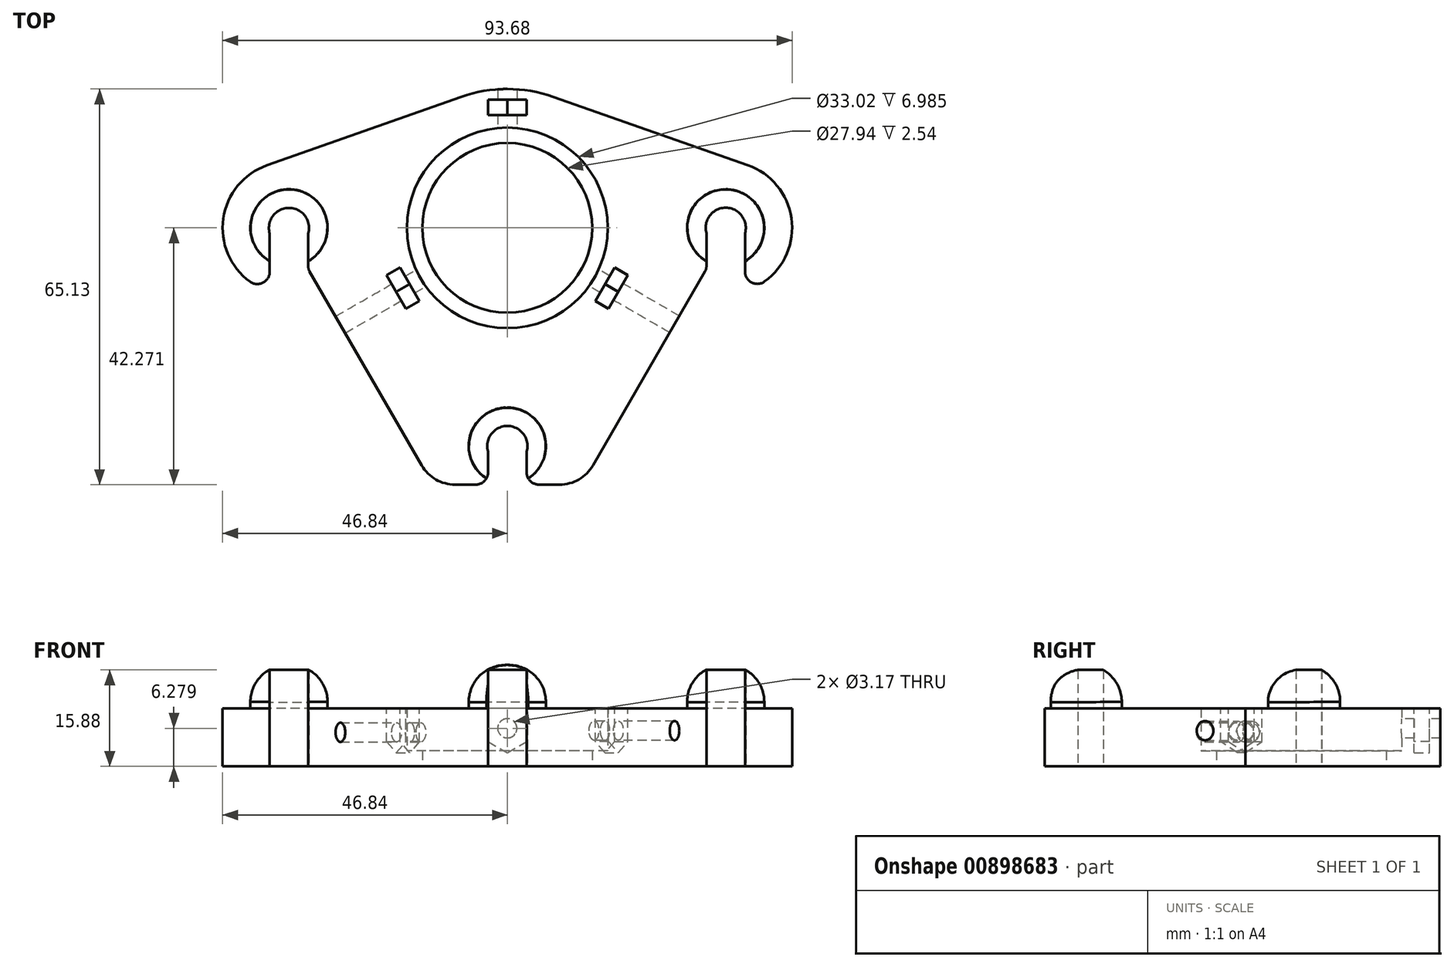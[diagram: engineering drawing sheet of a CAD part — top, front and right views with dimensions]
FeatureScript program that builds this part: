
annotation { "Feature Type Name" : "Feature", "Feature Type Description" : "" }
export const myFeature = defineFeature(function(context is Context, id is Id, definition is map)
    precondition{}
    {
        {
            var Q0;
            Q0=qCreatedBy(makeId("Top.planeOp"),FACE);
            var sketch = newSketch(context, id + "F0", { "sketchPlane" : qUnion([Q0])});
            skCircle(sketch, "E0", {"center": v(0, 35.92) * mm, "radius": 16.51 * mm});
            skArc(sketch, "E1.0", {"start": v(-39.55, 46.2) * mm, "mid": v(-46.73, 37.47) * mm, "end": v(-42.32, 27.05) * mm});
            skArc(sketch, "E2.0", {"start": v(7.59, 57.48) * mm, "mid": v(0, 58.78) * mm, "end": v(-7.6, 57.48) * mm});
            skArc(sketch, "E3.0", {"start": v(42.32, 27.08) * mm, "mid": v(46.73, 37.5) * mm, "end": v(39.55, 46.24) * mm});
            skLineSegment(sketch, "E4", {"start": v(-39.55, 46.2) * mm, "end": v(-7.6, 57.48) * mm});
            skLineSegment(sketch, "E5", {"start": v(7.59, 57.48) * mm, "end": v(39.55, 46.24) * mm});
            skCircle(sketch, "E6", {"center": v(-35.92, 35.92) * mm, "radius": 3.18 * mm, "construction": true});
            skCircle(sketch, "E7", {"center": v(35.92, 35.92) * mm, "radius": 3.18 * mm, "construction": true});
            skCircle(sketch, "E8", {"center": v(0, 0) * mm, "radius": 3.18 * mm, "construction": true});
            skLineSegment(sketch, "E9", {"start": v(-32.75, 35.92) * mm, "end": v(-32.75, 29.55) * mm});
            skLineSegment(sketch, "E10", {"start": v(-39.1, 35.92) * mm, "end": v(-39.1, 28.7) * mm});
            skLineSegment(sketch, "E11", {"start": v(-3.18, 0) * mm, "end": v(-3.17, -4.32) * mm});
            skLineSegment(sketch, "E12", {"start": v(3.17, 0) * mm, "end": v(3.17, -4.32) * mm});
            skLineSegment(sketch, "E13", {"start": v(32.75, 35.92) * mm, "end": v(32.75, 29.55) * mm});
            skLineSegment(sketch, "E14", {"start": v(39.1, 35.92) * mm, "end": v(39.1, 28.73) * mm});
            skCircle(sketch, "E15.0", {"center": v(0, 35.92) * mm, "radius": 13.97 * mm});
            skLineSegment(sketch, "E16", {"start": v(0, 35.92) * mm, "end": v(0, 52.43) * mm, "construction": true});
            skLineSegment(sketch, "E17", {"start": v(0, 35.92) * mm, "end": v(35.3, 15.54) * mm, "construction": true});
            skLineSegment(sketch, "E18", {"start": v(0, 35.92) * mm, "end": v(-35.36, 15.5) * mm, "construction": true});
            skCircle(sketch, "E19.cCircle", {"center": v(0, 35.92) * mm, "radius": 16.51 * mm, "construction": true});
            skLineSegment(sketch, "E19.0", {"start": v(9.53, 52.43) * mm, "end": v(19.06, 35.92) * mm, "construction": true});
            skLineSegment(sketch, "E19.1", {"start": v(19.06, 35.92) * mm, "end": v(9.53, 19.41) * mm, "construction": true});
            skLineSegment(sketch, "E19.2", {"start": v(9.53, 19.41) * mm, "end": v(-9.53, 19.41) * mm, "construction": true});
            skLineSegment(sketch, "E19.3", {"start": v(-9.53, 19.41) * mm, "end": v(-19.06, 35.92) * mm, "construction": true});
            skLineSegment(sketch, "E19.4", {"start": v(-19.06, 35.92) * mm, "end": v(-9.53, 52.43) * mm, "construction": true});
            skLineSegment(sketch, "E19.5", {"start": v(-9.53, 52.43) * mm, "end": v(9.53, 52.43) * mm, "construction": true});
            skPoint(sketch, "E19.0.midPoint", {"position": v(14.3, 44.18) * mm});
            skLineSegment(sketch, "E20", {"start": v(-35.92, 35.92) * mm, "end": v(35.92, 35.92) * mm, "construction": true});
            skCircle(sketch, "E21.0", {"center": v(0, 35.92) * mm, "radius": 31.75 * mm, "construction": true});
            skLineSegment(sketch, "E22", {"start": v(-32.54, 28.79) * mm, "end": v(-14.09, -3.17) * mm});
            skLineSegment(sketch, "E23", {"start": v(32.54, 28.79) * mm, "end": v(14.09, -3.18) * mm});
            skPoint(sketch, "E24.visualSharp", {"position": v(-32.75, 29.14) * mm});
            skArc(sketch, "E24.filletArc", {"start": v(-32.75, 29.55) * mm, "mid": v(-32.7, 29.15) * mm, "end": v(-32.54, 28.79) * mm});
            skPoint(sketch, "E25.visualSharp", {"position": v(32.75, 29.14) * mm});
            skArc(sketch, "E25.filletArc", {"start": v(32.54, 28.79) * mm, "mid": v(32.7, 29.15) * mm, "end": v(32.75, 29.55) * mm});
            skArc(sketch, "E26", {"start": v(3.17, -0.9) * mm, "mid": v(0, 3.3) * mm, "end": v(-3.18, -0.9) * mm});
            skArc(sketch, "E27", {"start": v(-32.75, 35) * mm, "mid": v(-35.92, 39.2) * mm, "end": v(-39.1, 35) * mm});
            skArc(sketch, "E28", {"start": v(39.1, 35.03) * mm, "mid": v(35.92, 39.24) * mm, "end": v(32.75, 35.03) * mm});
            skLineSegment(sketch, "E29", {"start": v(-8.6, -6.35) * mm, "end": v(-5.2, -6.35) * mm});
            skLineSegment(sketch, "E30.trimOffspring", {"start": v(5.2, -6.35) * mm, "end": v(8.6, -6.35) * mm});
            skPoint(sketch, "E31.visualSharp", {"position": v(-12.26, -6.35) * mm});
            skArc(sketch, "E31.filletArc", {"start": v(-14.09, -3.17) * mm, "mid": v(-11.77, -5.5) * mm, "end": v(-8.6, -6.35) * mm});
            skPoint(sketch, "E32.visualSharp", {"position": v(12.26, -6.35) * mm});
            skArc(sketch, "E32.filletArc", {"start": v(8.6, -6.35) * mm, "mid": v(11.77, -5.5) * mm, "end": v(14.09, -3.18) * mm});
            skPoint(sketch, "E33.visualSharp", {"position": v(-3.17, -6.35) * mm});
            skArc(sketch, "E33.filletArc", {"start": v(-5.2, -6.35) * mm, "mid": v(-3.77, -5.75) * mm, "end": v(-3.18, -4.32) * mm});
            skPoint(sketch, "E34.visualSharp", {"position": v(3.18, -6.35) * mm});
            skArc(sketch, "E34.filletArc", {"start": v(3.17, -4.32) * mm, "mid": v(3.77, -5.75) * mm, "end": v(5.2, -6.35) * mm});
            skPoint(sketch, "E35.visualSharp", {"position": v(-39.1, 25.46) * mm});
            skArc(sketch, "E35.filletArc", {"start": v(-42.32, 27.05) * mm, "mid": v(-40.2, 26.9) * mm, "end": v(-39.1, 28.7) * mm});
            skPoint(sketch, "E36.visualSharp", {"position": v(39.1, 25.49) * mm});
            skArc(sketch, "E36.filletArc", {"start": v(39.1, 28.73) * mm, "mid": v(40.2, 26.92) * mm, "end": v(42.32, 27.08) * mm});
            skSolve(sketch);
        }
        {
            var Q0;
            Q0=makeQuery(id+"F0.imprint","IMPRINT",FACE,{"disambiguationData":[TD([[makeQuery(id+"F0.imprint","IMPRINT",EDGE,{"derivedFrom":sQuery(id+"F0.wireOp",EDGE,"E0")}),-1.0]])]});
            extrude(context, id + "F1", {"entities" : qUnion([Q0]), "depth" : 9.52 * mm, "offsetDistance" : 25.4 * mm});
        }
        {
            var Q0;
            Q0=makeQuery(id+"F0.imprint","IMPRINT",FACE,{"disambiguationData":[TD([[makeQuery(id+"F0.imprint","IMPRINT",EDGE,{"derivedFrom":sQuery(id+"F0.wireOp",EDGE,"E0")}),1.0]])]});
            extrude(context, id + "F2", {"entities" : qUnion([Q0]), "operationType" : NewBodyOperationType.ADD, "depth" : 2.54 * mm, "hasOffset" : true, "offsetDistance" : 6.35 * mm});
        }
        {
            var Q0;
            Q0=makeQuery(id+"F1.opExtrude","CAP_FACE",FACE,{"disambiguationData":[OSD([sQuery(id+"F0.wireOp",EDGE,"EjYE8rPL-0voM-13ep-dpKR-Yhmu4oC0fMjX"),sQuery(id+"F0.wireOp",EDGE,"BDsdlpYl-4XZS-kb72-SQzJ-jy24um5DGsSm"),sQuery(id+"F0.wireOp",EDGE,"zDj9rnkT-zBYQ-YRrf-FuGE-prHvdQQL9E0l"),sQuery(id+"F0.wireOp",EDGE,"E0"),sQuery(id+"F0.wireOp",EDGE,"E1.0"),sQuery(id+"F0.wireOp",EDGE,"E2.0"),sQuery(id+"F0.wireOp",EDGE,"E3.0"),sQuery(id+"F0.wireOp",EDGE,"02fbeba7-076e-4ed0-9f02-67362b93dccf.0"),sQuery(id+"F0.wireOp",EDGE,"E4"),sQuery(id+"F0.wireOp",EDGE,"E5"),sQuery(id+"F0.wireOp",EDGE,"O9yRHGw0-B6N5-WUBC-CqYZ-9fVMz9zkHXct"),sQuery(id+"F0.wireOp",EDGE,"bXI39tXD-kIKO-QA8d-uo1d-AjNWw4kzWSzn"),sQuery(id+"F0.wireOp",EDGE,"E9"),sQuery(id+"F0.wireOp",EDGE,"E10"),sQuery(id+"F0.wireOp",EDGE,"E11"),sQuery(id+"F0.wireOp",EDGE,"E12"),sQuery(id+"F0.wireOp",EDGE,"1b80de2d-6fcf-4166-8bd7-bc7520118ab3.trimOffspring"),sQuery(id+"F0.wireOp",EDGE,"c2b8b45b-57a7-46a8-b7ff-993cbbd2993e.trimOffspring"),sQuery(id+"F0.wireOp",EDGE,"9e57da74-859c-4f91-937b-fdcaf8afdda5.filletArc"),sQuery(id+"F0.wireOp",EDGE,"30e6a12d-ff62-4460-809b-2951cf116d4f.filletArc"),sQuery(id+"F0.wireOp",EDGE,"3d167f00-72a4-4ff5-8a6d-0d591a0e7773.filletArc"),sQuery(id+"F0.wireOp",EDGE,"E13"),sQuery(id+"F0.wireOp",EDGE,"E14"),sQuery(id+"F0.wireOp",EDGE,"02ed80ea-b338-46f1-988c-5186e078d909.trimOffspring"),sQuery(id+"F0.wireOp",EDGE,"3LgmcLzA-5pnU-fFz7-q1u9-bpeBtAsCO3An"),sQuery(id+"F0.wireOp",EDGE,"4eo9xTR6-c1Fu-en91-zOid-S4E7wj55DmDX"),sQuery(id+"F0.wireOp",EDGE,"5048e359-dd0b-4d89-8e95-103b38747b91.filletArc"),sQuery(id+"F0.wireOp",EDGE,"0de4be46-af92-408f-a28e-b5eb566cc358.filletArc"),sQuery(id+"F0.wireOp",EDGE,"cd97e584-8722-4711-bad1-4d169eb79cda.filletArc"),sQuery(id+"F0.wireOp",EDGE,"a80f9f6f-3806-41d0-9fd0-596e0330244b.filletArc"),sQuery(id+"F0.wireOp",EDGE,"743a1c7c-530f-41f0-bede-06812bb20fe3.filletArc")])],"isStart":false});
            var sketch = newSketch(context, id + "F3", { "sketchPlane" : qUnion([Q0])});
            skCircle(sketch, "E37", {"center": v(-35.92, 35.92) * mm, "radius": 6.35 * mm});
            skCircle(sketch, "E38", {"center": v(35.92, 35.92) * mm, "radius": 6.35 * mm});
            skCircle(sketch, "E39", {"center": v(0, 0) * mm, "radius": 6.35 * mm});
            skSolve(sketch);
        }
        {
            var Q0;
            Q0=makeQuery(id+"F1.opExtrude","CAP_FACE",FACE,{"disambiguationData":[OSD([sQuery(id+"F0.wireOp",EDGE,"EjYE8rPL-0voM-13ep-dpKR-Yhmu4oC0fMjX"),sQuery(id+"F0.wireOp",EDGE,"BDsdlpYl-4XZS-kb72-SQzJ-jy24um5DGsSm"),sQuery(id+"F0.wireOp",EDGE,"zDj9rnkT-zBYQ-YRrf-FuGE-prHvdQQL9E0l"),sQuery(id+"F0.wireOp",EDGE,"E0"),sQuery(id+"F0.wireOp",EDGE,"E1.0"),sQuery(id+"F0.wireOp",EDGE,"E2.0"),sQuery(id+"F0.wireOp",EDGE,"E3.0"),sQuery(id+"F0.wireOp",EDGE,"02fbeba7-076e-4ed0-9f02-67362b93dccf.0"),sQuery(id+"F0.wireOp",EDGE,"E4"),sQuery(id+"F0.wireOp",EDGE,"E5"),sQuery(id+"F0.wireOp",EDGE,"O9yRHGw0-B6N5-WUBC-CqYZ-9fVMz9zkHXct"),sQuery(id+"F0.wireOp",EDGE,"bXI39tXD-kIKO-QA8d-uo1d-AjNWw4kzWSzn"),sQuery(id+"F0.wireOp",EDGE,"E9"),sQuery(id+"F0.wireOp",EDGE,"E10"),sQuery(id+"F0.wireOp",EDGE,"E11"),sQuery(id+"F0.wireOp",EDGE,"E12"),sQuery(id+"F0.wireOp",EDGE,"1b80de2d-6fcf-4166-8bd7-bc7520118ab3.trimOffspring"),sQuery(id+"F0.wireOp",EDGE,"c2b8b45b-57a7-46a8-b7ff-993cbbd2993e.trimOffspring"),sQuery(id+"F0.wireOp",EDGE,"9e57da74-859c-4f91-937b-fdcaf8afdda5.filletArc"),sQuery(id+"F0.wireOp",EDGE,"2f08ad09-a47d-42bd-8f0e-b7f58f6490e4.filletArc"),sQuery(id+"F0.wireOp",EDGE,"30e6a12d-ff62-4460-809b-2951cf116d4f.filletArc"),sQuery(id+"F0.wireOp",EDGE,"3d167f00-72a4-4ff5-8a6d-0d591a0e7773.filletArc"),sQuery(id+"F0.wireOp",EDGE,"E13"),sQuery(id+"F0.wireOp",EDGE,"E14"),sQuery(id+"F0.wireOp",EDGE,"02ed80ea-b338-46f1-988c-5186e078d909.trimOffspring"),sQuery(id+"F0.wireOp",EDGE,"bfc3d6b4-ed7b-404a-8939-94d15189dd00.filletArc"),sQuery(id+"F0.wireOp",EDGE,"d06de643-c4a7-4e1d-b592-4d839de3a7a0.filletArc")])],"isStart":false});
            var sketch = newSketch(context, id + "F4", { "sketchPlane" : qUnion([Q0])});
            skLineSegment(sketch, "E40", {"start": v(-3.18, 54.46) * mm, "end": v(-3.18, 57) * mm});
            skLineSegment(sketch, "E41", {"start": v(-3.18, 57) * mm, "end": v(3.17, 57) * mm});
            skLineSegment(sketch, "E42", {"start": v(3.17, 57) * mm, "end": v(3.17, 54.46) * mm});
            skLineSegment(sketch, "E43", {"start": v(3.18, 54.46) * mm, "end": v(-3.18, 54.46) * mm});
            skLineSegment(sketch, "E44", {"start": v(0, 52.43) * mm, "end": v(0, 54.46) * mm});
            skLineSegment(sketch, "E45.1.0", {"start": v(-17.65, 29.4) * mm, "end": v(-14.47, 23.9) * mm});
            skLineSegment(sketch, "E45.1.1", {"start": v(-19.85, 28.13) * mm, "end": v(-17.65, 29.4) * mm});
            skLineSegment(sketch, "E45.1.2", {"start": v(-16.67, 22.63) * mm, "end": v(-19.85, 28.13) * mm});
            skLineSegment(sketch, "E45.1.3", {"start": v(-14.47, 23.9) * mm, "end": v(-16.67, 22.63) * mm});
            skLineSegment(sketch, "E45.2.0", {"start": v(14.47, 23.9) * mm, "end": v(17.65, 29.4) * mm});
            skLineSegment(sketch, "E45.2.1", {"start": v(16.67, 22.63) * mm, "end": v(14.47, 23.9) * mm});
            skLineSegment(sketch, "E45.2.2", {"start": v(19.85, 28.13) * mm, "end": v(16.67, 22.63) * mm});
            skLineSegment(sketch, "E45.2.3", {"start": v(17.65, 29.4) * mm, "end": v(19.85, 28.13) * mm});
            skPoint(sketch, "E45.center", {"position": v(0, 35.92) * mm});
            skSolve(sketch);
        }
        {
            var Q0;
            Q0=makeQuery(id+"F4.imprint","IMPRINT",FACE,{"disambiguationData":[TD([[makeQuery(id+"F4.imprint","IMPRINT",EDGE,{"derivedFrom":sQuery(id+"F4.wireOp",EDGE,"E45.2.0")}),-1.0]])]});
            var Q1;
            {var subQ3=sQuery(id+"F4.wireOp",EDGE,"E40");Q1=makeQuery(id+"F4.imprint","IMPRINT",FACE,{"disambiguationData":[TD([[makeQuery(id+"F4.imprint","IMPRINT",EDGE,{"derivedFrom":subQ3}),-1.0]])]});}
            var Q2;
            Q2=makeQuery(id+"F4.imprint","IMPRINT",FACE,{"disambiguationData":[TD([[makeQuery(id+"F4.imprint","IMPRINT",EDGE,{"derivedFrom":sQuery(id+"F4.wireOp",EDGE,"E45.1.0")}),-1.0]])]});
            extrude(context, id + "F5", {"entities" : qUnion([Q0, Q1, Q2]), "operationType" : NewBodyOperationType.REMOVE, "oppositeDirection" : true, "depth" : 8.64 * mm, "offsetDistance" : 25.4 * mm});
        }
        {
            var Q0;
            Q0=makeQuery(id+"F5.boolean.opBoolean","COPY",EDGE,{"derivedFrom":makeQuery(id+"F5.opExtrude","CAP_EDGE",EDGE,{"disambiguationData":[OSD([sQuery(id+"F4.wireOp",EDGE,"E45.1.1")])],"isStart":false})});
            var Q1;
            Q1=makeQuery(id+"F5.boolean.opBoolean","COPY",EDGE,{"derivedFrom":makeQuery(id+"F5.opExtrude","CAP_EDGE",EDGE,{"disambiguationData":[OSD([sQuery(id+"F4.wireOp",EDGE,"E45.1.3")])],"isStart":false})});
            var Q2;
            Q2=makeQuery(id+"F5.boolean.opBoolean","COPY",EDGE,{"derivedFrom":makeQuery(id+"F5.opExtrude","CAP_EDGE",EDGE,{"disambiguationData":[OSD([sQuery(id+"F4.wireOp",EDGE,"E40")])],"isStart":false})});
            var Q3;
            Q3=makeQuery(id+"F5.boolean.opBoolean","COPY",EDGE,{"derivedFrom":makeQuery(id+"F5.opExtrude","CAP_EDGE",EDGE,{"disambiguationData":[OSD([sQuery(id+"F4.wireOp",EDGE,"E42")])],"isStart":false})});
            var Q4;
            Q4=makeQuery(id+"F5.boolean.opBoolean","COPY",EDGE,{"derivedFrom":makeQuery(id+"F5.opExtrude","CAP_EDGE",EDGE,{"disambiguationData":[OSD([sQuery(id+"F4.wireOp",EDGE,"E45.2.3")])],"isStart":false})});
            var Q5;
            Q5=makeQuery(id+"F5.boolean.opBoolean","COPY",EDGE,{"derivedFrom":makeQuery(id+"F5.opExtrude","CAP_EDGE",EDGE,{"disambiguationData":[OSD([sQuery(id+"F4.wireOp",EDGE,"E45.2.1")])],"isStart":false})});
            chamfer(context, id + "F6", {"entities" : qUnion([Q0, Q1, Q2, Q3, Q4, Q5]), "chamferType" : ChamferType.OFFSET_ANGLE, "width" : 3.17 * mm, "oppositeDirection" : false, "angle" : 60 * degree, "tangentPropagation" : true});
        }
        {
            var Q0;
            Q0=makeQuery(id+"F5.boolean.opBoolean","COPY",FACE,{"derivedFrom":makeQuery(id+"F5.opExtrude","SWEPT_FACE",FACE,{"disambiguationData":[OSD([sQuery(id+"F4.wireOp",EDGE,"E41")])]})});
            var sketch = newSketch(context, id + "F7", { "sketchPlane" : qUnion([Q0])});
            skLineSegment(sketch, "E46", {"start": v(3.17, 4.06) * mm, "end": v(0, 2.23) * mm});
            skLineSegment(sketch, "E47", {"start": v(0, 2.23) * mm, "end": v(-3.18, 4.06) * mm});
            skLineSegment(sketch, "E48", {"start": v(-3.17, 4.06) * mm, "end": v(-3.17, 7.73) * mm});
            skLineSegment(sketch, "E49", {"start": v(3.18, 7.73) * mm, "end": v(3.18, 4.06) * mm});
            skLineSegment(sketch, "E50", {"start": v(3.17, 7.73) * mm, "end": v(0, 9.55) * mm});
            skPoint(sketch, "E50.endSnap0", {"position": v(0, 9.53) * mm});
            skLineSegment(sketch, "E51", {"start": v(0, 9.55) * mm, "end": v(-3.17, 7.73) * mm});
            skLineSegment(sketch, "E52", {"start": v(0, 2.23) * mm, "end": v(0, 6.28) * mm, "construction": true});
            skLineSegment(sketch, "E53", {"start": v(0, 6.28) * mm, "end": v(3.17, 4.06) * mm, "construction": true});
            skLineSegment(sketch, "E54", {"start": v(0, 6.28) * mm, "end": v(-3.18, 4.06) * mm, "construction": true});
            skLineSegment(sketch, "E55", {"start": v(0, 6.28) * mm, "end": v(-3.17, 7.73) * mm, "construction": true});
            skLineSegment(sketch, "E56", {"start": v(0, 6.28) * mm, "end": v(3.17, 7.73) * mm, "construction": true});
            skLineSegment(sketch, "E57", {"start": v(0, 6.28) * mm, "end": v(0, 9.55) * mm, "construction": true});
            skCircle(sketch, "E58", {"center": v(0, 6.28) * mm, "radius": 1.59 * mm});
            skSolve(sketch);
        }
        {
            var Q0;
            Q0=makeQuery(id+"F5.boolean.opBoolean","COPY",FACE,{"derivedFrom":makeQuery(id+"F5.opExtrude","SWEPT_FACE",FACE,{"disambiguationData":[OSD([sQuery(id+"F4.wireOp",EDGE,"E45.1.2")])]})});
            var sketch = newSketch(context, id + "F8", { "sketchPlane" : qUnion([Q0])});
            skLineSegment(sketch, "E59", {"start": v(34.2, 3.78) * mm, "end": v(31.03, 1.94) * mm});
            skLineSegment(sketch, "E60", {"start": v(31.03, 1.94) * mm, "end": v(27.86, 3.78) * mm});
            skLineSegment(sketch, "E61", {"start": v(27.86, 3.78) * mm, "end": v(27.86, 7.44) * mm});
            skLineSegment(sketch, "E62", {"start": v(34.2, 7.44) * mm, "end": v(34.2, 3.78) * mm});
            skLineSegment(sketch, "E63", {"start": v(34.2, 7.44) * mm, "end": v(31.03, 9.26) * mm});
            skLineSegment(sketch, "E64", {"start": v(31.03, 9.26) * mm, "end": v(27.86, 7.44) * mm});
            skCircle(sketch, "E65", {"center": v(31.03, 5.6) * mm, "radius": 1.59 * mm});
            skSolve(sketch);
        }
        {
            var Q0;
            Q0=makeQuery(id+"F5.boolean.opBoolean","COPY",FACE,{"derivedFrom":makeQuery(id+"F5.opExtrude","SWEPT_FACE",FACE,{"disambiguationData":[OSD([sQuery(id+"F4.wireOp",EDGE,"E45.2.2")])]})});
            var sketch = newSketch(context, id + "F9", { "sketchPlane" : qUnion([Q0])});
            skLineSegment(sketch, "E66", {"start": v(-27.95, 4.06) * mm, "end": v(-31.12, 2.24) * mm});
            skLineSegment(sketch, "E67", {"start": v(-31.12, 2.24) * mm, "end": v(-34.28, 4.06) * mm});
            skLineSegment(sketch, "E68", {"start": v(-34.28, 4.06) * mm, "end": v(-34.28, 7.72) * mm});
            skLineSegment(sketch, "E69", {"start": v(-27.95, 7.72) * mm, "end": v(-27.95, 4.06) * mm});
            skLineSegment(sketch, "E70", {"start": v(-27.95, 7.72) * mm, "end": v(-31.12, 9.55) * mm});
            skLineSegment(sketch, "E71", {"start": v(-31.12, 9.55) * mm, "end": v(-34.28, 7.72) * mm});
            skCircle(sketch, "E72", {"center": v(-31.12, 5.9) * mm, "radius": 1.59 * mm});
            skLineSegment(sketch, "E73", {"start": v(-31.12, 2.24) * mm, "end": v(-31.12, 5.9) * mm, "construction": true});
            skLineSegment(sketch, "E74", {"start": v(-31.12, 5.9) * mm, "end": v(-34.28, 4.06) * mm, "construction": true});
            skLineSegment(sketch, "E75", {"start": v(-31.12, 9.55) * mm, "end": v(-31.12, 5.9) * mm, "construction": true});
            skLineSegment(sketch, "E76", {"start": v(-27.95, 7.72) * mm, "end": v(-31.12, 5.9) * mm, "construction": true});
            skSolve(sketch);
        }
        {
            var Q0;
            Q0=makeQuery(id+"F7.imprint","IMPRINT",FACE,{"disambiguationData":[TD([[makeQuery(id+"F7.imprint","IMPRINT",EDGE,{"derivedFrom":sQuery(id+"F7.wireOp",EDGE,"E58")}),1.0]])]});
            extrude(context, id + "F10", {"entities" : qUnion([Q0]), "operationType" : NewBodyOperationType.REMOVE, "oppositeDirection" : true, "depth" : 10.16 * mm, "offsetDistance" : 25.4 * mm, "symmetric" : true});
        }
        {
            var Q0;
            Q0=makeQuery(id+"F8.imprint","IMPRINT",FACE,{"disambiguationData":[TD([[makeQuery(id+"F8.imprint","IMPRINT",EDGE,{"derivedFrom":sQuery(id+"F8.wireOp",EDGE,"E65")}),1.0]])]});
            var Q1;
            Q1=sQuery(id+"F8.wireOp",EDGE,"E65");
            extrude(context, id + "F11", {"entities" : qUnion([Q0]), "operationType" : NewBodyOperationType.REMOVE, "surfaceEntities" : qUnion([Q1]), "oppositeDirection" : true, "depth" : 40.64 * mm, "offsetDistance" : 25.4 * mm, "symmetric" : true});
        }
        {
            var Q0;
            Q0=makeQuery(id+"F9.imprint","IMPRINT",FACE,{"disambiguationData":[TD([[makeQuery(id+"F9.imprint","IMPRINT",EDGE,{"derivedFrom":sQuery(id+"F9.wireOp",EDGE,"E72")}),1.0]])]});
            var Q1;
            Q1=sQuery(id+"F9.wireOp",EDGE,"E72");
            extrude(context, id + "F12", {"entities" : qUnion([Q0]), "operationType" : NewBodyOperationType.REMOVE, "surfaceEntities" : qUnion([Q1]), "oppositeDirection" : true, "depth" : 40.64 * mm, "offsetDistance" : 25.4 * mm, "symmetric" : true});
        }
        {
            var Q0;
            {var subQ5=makeQuery(id+"F1.opExtrude","CAP_EDGE",EDGE,{"disambiguationData":[OSD([sQuery(id+"F0.wireOp",EDGE,"E27")])],"isStart":false});Q0=makeQuery(id+"F3.imprint","IMPRINT",FACE,{"disambiguationData":[TD([[makeQuery(id+"F3.imprint","IMPRINT",EDGE,{"derivedFrom":subQ5}),-1.0]])]});}
            var Q1;
            {var subQ5=makeQuery(id+"F1.opExtrude","CAP_EDGE",EDGE,{"disambiguationData":[OSD([sQuery(id+"F0.wireOp",EDGE,"E28")])],"isStart":false});Q1=makeQuery(id+"F3.imprint","IMPRINT",FACE,{"disambiguationData":[TD([[makeQuery(id+"F3.imprint","IMPRINT",EDGE,{"derivedFrom":subQ5}),-1.0]])]});}
            var Q2;
            {var subQ1=makeQuery(id+"F1.opExtrude","CAP_EDGE",EDGE,{"disambiguationData":[OSD([sQuery(id+"F0.wireOp",EDGE,"E11")])],"isStart":false});Q2=makeQuery(id+"F3.imprint","IMPRINT",FACE,{"disambiguationData":[TD([[makeQuery(id+"F3.imprint","IMPRINT",EDGE,{"derivedFrom":subQ1}),-1.0]])]});}
            extrude(context, id + "F13", {"entities" : qUnion([Q0, Q1, Q2]), "operationType" : NewBodyOperationType.ADD, "depth" : 6.35 * mm, "offsetDistance" : 25.4 * mm});
        }
        {
            var Q0;
            Q0=makeQuery(id+"F13.opExtrude","CAP_EDGE",EDGE,{"disambiguationData":[OSD([sQuery(id+"F3.wireOp",EDGE,"E37")])],"isStart":false});
            var Q1;
            Q1=makeQuery(id+"F13.opExtrude","CAP_EDGE",EDGE,{"disambiguationData":[OSD([sQuery(id+"F3.wireOp",EDGE,"E38")])],"isStart":false});
            var Q2;
            Q2=makeQuery(id+"F13.opExtrude","CAP_EDGE",EDGE,{"disambiguationData":[OSD([sQuery(id+"F3.wireOp",EDGE,"E39")])],"isStart":false});
            fillet(context, id + "F14", {"entities" : qUnion([Q0, Q1, Q2]), "radius" : 6.1 * mm, "tangentPropagation" : true, "allowEdgeOverflow" : false});
        }
    });
